# Revit family: 1398020 - Kinzo 140 - Bronze
name_source: partatom
category: Lighting Fixtures
revit_build: Autodesk Revit 2018 (Build: 20170223_1515(x64)
units: mm (PartAtom-declared; Revit-internal decimal feet)

## family parameters
Always vertical = Yes
Cut with Voids When Loaded = No
Host = Ceiling
Light Source = Yes
OmniClass Number = 23.80.70.11
OmniClass Title = Luminaries for Internal Lighting
Part Type = Normal
Room Calculation Point = No
Round Connector Dimension = Use Diameter
Shared = No

## types (2) — shared parameters
Color Filter = 16777215
Dimmable = Yes
Dimming Lamp Color Temperature Shift = <None>
Dimming Method = Phase - Leading & Trailing Edge
Electrical Class = 1
Length of supplied cable = Not Applicable
Light Source Fixed = Yes
Manufacturer URL - Europe and Rest of World = www.astrolighting.com
Manufacturer URL - North America = us.astrolighting.com
Max Drop (pendants) = Not Applicable
Product Name = Kinzo 140
Product Weight (KG) = 1 mm  [stored 0.00328084 ft]

## per-type parameters (varying)
| type | ADA compliant | Apparent Load | Driver Included | Driver Required | Efficacy (lm/w) | Lamp | Location / IP Rating | Main Finish | Main Material | Photometric Web File | Power (Watts) | Product CCT | Product CRI | Product Dimensions (MM) | Product Location | Product SKU | Tilt Angle |
| CE | Not Applicable | 12 VA | Yes (Integral) | No (AC LED) | 61 | LED | IP20 | Bronze | Metal - Aluminium | 1398020_Kinzo 140_Photometry_IES_Iss.01.ies | 12.5 | 2700K | 80 | 140 x 110 x 110 | Indoor | 1398020 | 0.00° |
| ETL |  | 13 VA | Yes | No | 64 | Lumens AC LED Module |  | Textured White | Aluminium | generic | 12W | 2700K / 3000K | 80/ 90 | 140x110x110 |  | 1398017 | 90.00° |

note: [stored X ft] marks values corroborated as IEEE doubles in the binary element streams (Revit-internal decimal feet)

## geometry (parser evidence)
native form markers: Sweep x1
no freeform markers — native parametric forms only
